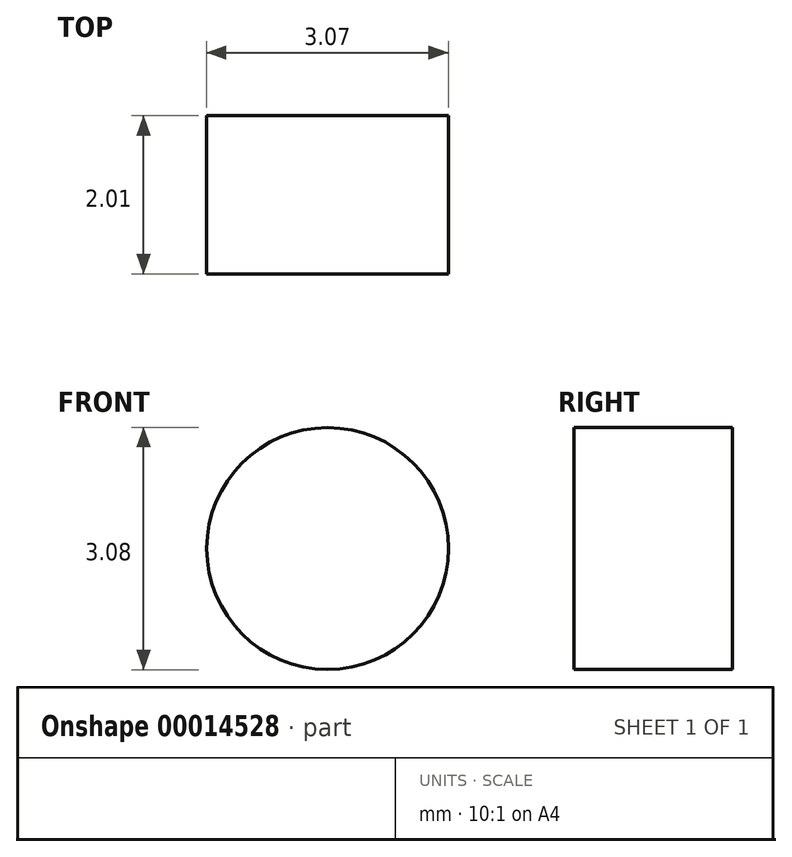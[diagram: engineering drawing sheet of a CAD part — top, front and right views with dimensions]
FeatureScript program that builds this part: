
annotation { "Feature Type Name" : "Feature", "Feature Type Description" : "" }
export const myFeature = defineFeature(function(context is Context, id is Id, definition is map)
    precondition{}
    {
        {
            var Q0;
            Q0=qCreatedBy(makeId("Front.planeOp"),FACE);
            var sketch = newSketch(context, id + "F0", { "sketchPlane" : qUnion([Q0])});
            skCircle(sketch, "E0", {"center": v(-16.97, 9.84) * mm, "radius": 1.54 * mm});
            skSolve(sketch);
        }
        {
            var Q0;
            Q0 = qSketchRegion(id + "F0", true);
            extrude(context, id + "F1", {"entities" : qUnion([Q0]), "depth" : 2 * mm});
        }
    });
